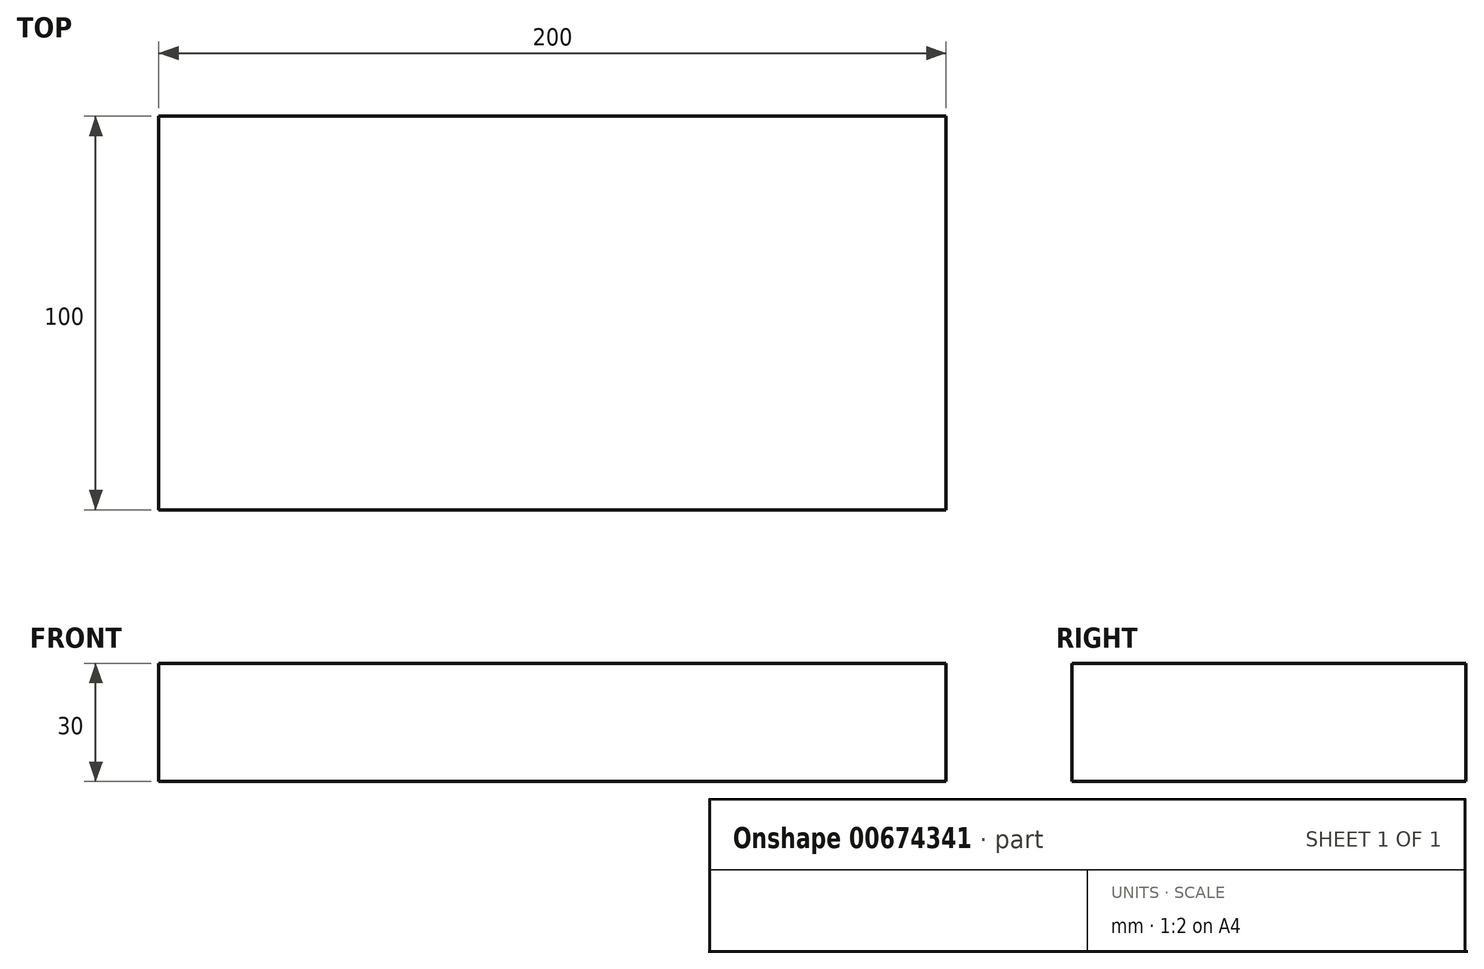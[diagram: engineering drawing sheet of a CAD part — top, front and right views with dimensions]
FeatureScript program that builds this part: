
annotation { "Feature Type Name" : "Feature", "Feature Type Description" : "" }
export const myFeature = defineFeature(function(context is Context, id is Id, definition is map)
    precondition{}
    {
        {
            var Q0;
            Q0=qCreatedBy(makeId("Top.planeOp"),FACE);
            var sketch = newSketch(context, id + "F0", { "sketchPlane" : qUnion([Q0])});
            skLineSegment(sketch, "E0.bottom", {"start": v(-100, -52.86) * mm, "end": v(100, -52.86) * mm});
            skLineSegment(sketch, "E0.top", {"start": v(-100, 47.14) * mm, "end": v(100, 47.14) * mm});
            skLineSegment(sketch, "E0.left", {"start": v(-100, -52.86) * mm, "end": v(-100, 47.14) * mm});
            skLineSegment(sketch, "E0.right", {"start": v(100, -52.86) * mm, "end": v(100, 47.14) * mm});
            skPoint(sketch, "E0.middle", {"position": v(0, -2.86) * mm});
            skSolve(sketch);
        }
        {
            var Q0;
            Q0=makeQuery(id+"F0.imprint","IMPRINT",FACE,{"disambiguationData":[TD([[makeQuery(id+"F0.imprint","IMPRINT",EDGE,{"derivedFrom":sQuery(id+"F0.wireOp",EDGE,"E0.bottom")}),1.0]])]});
            extrude(context, id + "F1", {"entities" : qUnion([Q0]), "oppositeDirection" : true, "depth" : 30 * mm, "offsetDistance" : 25 * mm});
        }
    });
